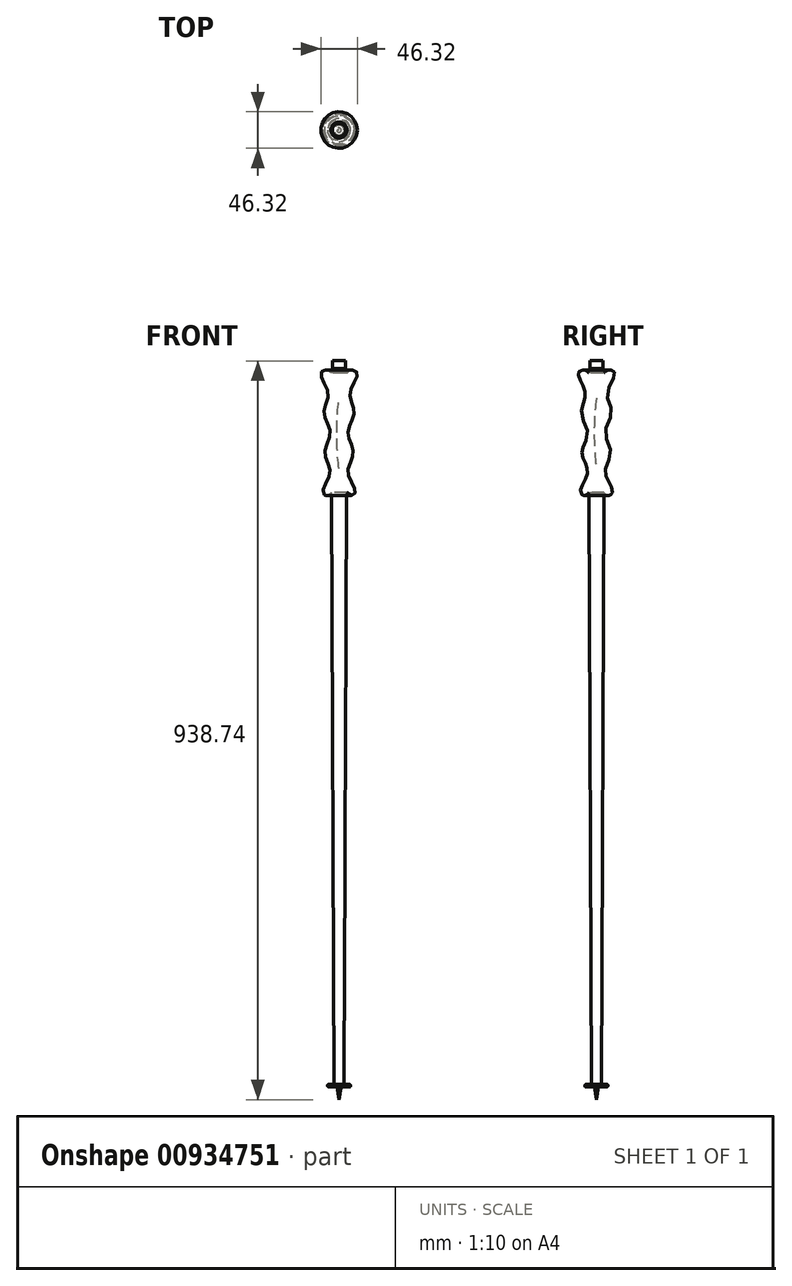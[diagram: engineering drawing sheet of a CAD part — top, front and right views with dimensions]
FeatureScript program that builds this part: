
annotation { "Feature Type Name" : "Feature", "Feature Type Description" : "" }
export const myFeature = defineFeature(function(context is Context, id is Id, definition is map)
    precondition{}
    {
        {
            var Q0;
            Q0=qCreatedBy(makeId("Front.planeOp"),FACE);
            var sketch = newSketch(context, id + "F0", { "sketchPlane" : qUnion([Q0])});
            skLineSegment(sketch, "E0", {"start": v(0, 848.21) * mm, "end": v(0, -75.29) * mm});
            skLineSegment(sketch, "E1", {"start": v(0, -75.29) * mm, "end": v(2.67, -59.13) * mm});
            skLineSegment(sketch, "E2", {"start": v(10.16, 848.21) * mm, "end": v(0, 848.21) * mm});
            skLineSegment(sketch, "E3", {"start": v(10.16, 848.21) * mm, "end": v(6.35, -55.9) * mm});
            skLineSegment(sketch, "E4", {"start": v(6.35, -55.9) * mm, "end": v(13.38, -55.93) * mm});
            skLineSegment(sketch, "E5", {"start": v(14.65, -57.2) * mm, "end": v(14.65, -57.94) * mm});
            skLineSegment(sketch, "E6", {"start": v(13.88, -58.7) * mm, "end": v(3.17, -58.7) * mm});
            skPoint(sketch, "E7.visualSharp", {"position": v(14.65, -55.93) * mm});
            skArc(sketch, "E7.filletArc", {"start": v(14.65, -57.2) * mm, "mid": v(14.28, -56.3) * mm, "end": v(13.38, -55.93) * mm});
            skPoint(sketch, "E8.visualSharp", {"position": v(14.65, -58.7) * mm});
            skArc(sketch, "E8.filletArc", {"start": v(13.88, -58.7) * mm, "mid": v(14.42, -58.48) * mm, "end": v(14.65, -57.94) * mm});
            skPoint(sketch, "E9.visualSharp", {"position": v(2.74, -58.7) * mm});
            skArc(sketch, "E9.filletArc", {"start": v(3.17, -58.7) * mm, "mid": v(2.84, -58.83) * mm, "end": v(2.67, -59.13) * mm});
            skFitSpline(sketch, "E10", {"points": [v(10.16, 848.21) * mm, v(22.95, 848.21) * mm, v(14, 822.81) * mm, v(19.3, 797.41) * mm, v(11.13, 772.01) * mm, v(18.18, 746.61) * mm, v(11.42, 721.21) * mm, v(20.46, 695.81) * mm, v(9.52, 695.81) * mm, v(10.16, 848.21) * mm]});
            skSolve(sketch);
        }
        {
            var Q0;
            Q0=qSketchRegion(id+"F0",true);
            var Q1;
            Q1=sQuery(id+"F0.wireOp",EDGE,"E0");
            revolve(context, id + "F1", {"entities" : qUnion([Q0]), "axis" : qUnion([Q1]), "revolveType" : RevolveType.FULL});
        }
        {
            var Q0;
            Q0=makeQuery(id+"F1.opRevolve","SWEPT_FACE",FACE,{"disambiguationData":[OSD([sQuery(id+"F0.wireOp",EDGE,"E2")])]});
            var sketch = newSketch(context, id + "F2", { "sketchPlane" : qUnion([Q0])});
            skLineSegment(sketch, "E11.bottom", {"start": v(-7.62, 6.72) * mm, "end": v(7.62, 6.72) * mm});
            skLineSegment(sketch, "E11.top", {"start": v(-7.62, -6.72) * mm, "end": v(7.62, -6.72) * mm});
            skLineSegment(sketch, "E11.left", {"start": v(-7.62, 6.72) * mm, "end": v(-7.62, -6.72) * mm});
            skLineSegment(sketch, "E11.right", {"start": v(7.62, 6.72) * mm, "end": v(7.62, -6.72) * mm});
            skPoint(sketch, "E11.middle", {"position": v(0, 0) * mm});
            skSolve(sketch);
        }
        {
            var Q0;
            Q0=qSketchRegion(id+"F2",true);
            extrude(context, id + "F3", {"entities" : qUnion([Q0]), "operationType" : NewBodyOperationType.ADD, "depth" : 5.08 * mm});
        }
        {
            var Q0;
            Q0=makeQuery(id+"F3.opExtrude","CAP_FACE",FACE,{"disambiguationData":[OSD([sQuery(id+"F2.wireOp",EDGE,"E11.bottom"),sQuery(id+"F2.wireOp",EDGE,"E11.top"),sQuery(id+"F2.wireOp",EDGE,"E11.left"),sQuery(id+"F2.wireOp",EDGE,"E11.right")])],"isStart":false});
            var sketch = newSketch(context, id + "F4", { "sketchPlane" : qUnion([Q0])});
            skCircle(sketch, "E12", {"center": v(0, 0) * mm, "radius": 8.41 * mm});
            skSolve(sketch);
        }
        {
            var Q0;
            Q0=qSketchRegion(id+"F4",true);
            extrude(context, id + "F5", {"entities" : qUnion([Q0]), "operationType" : NewBodyOperationType.ADD, "depth" : 10.16 * mm});
        }
    });
